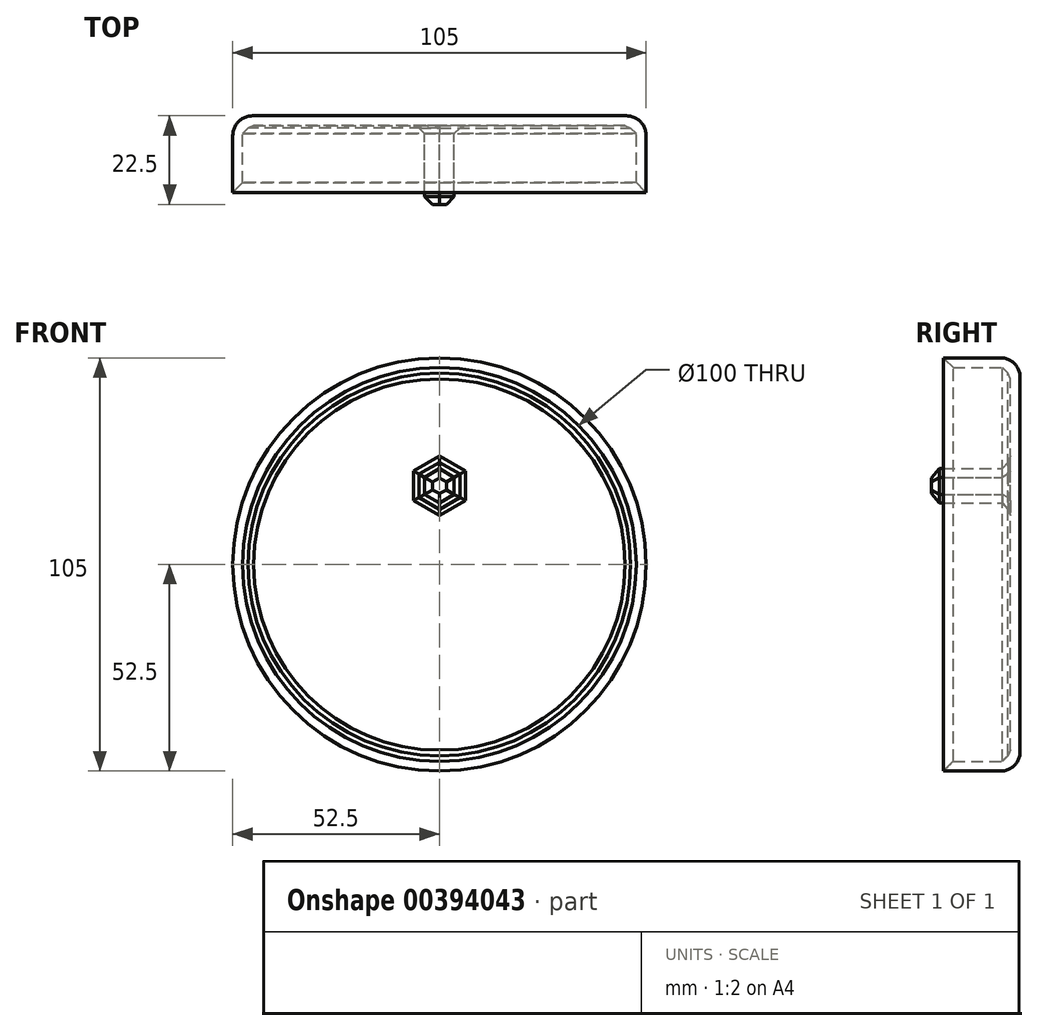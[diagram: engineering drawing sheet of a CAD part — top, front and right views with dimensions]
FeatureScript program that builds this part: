
annotation { "Feature Type Name" : "Feature", "Feature Type Description" : "" }
export const myFeature = defineFeature(function(context is Context, id is Id, definition is map)
    precondition{}
    {
        {
            var Q0;
            Q0=qCreatedBy(makeId("Front.planeOp"),FACE);
            var sketch = newSketch(context, id + "F0", { "sketchPlane" : qUnion([Q0])});
            skCircle(sketch, "E0", {"center": v(0, 0) * mm, "radius": 52.5 * mm});
            skSolve(sketch);
        }
        {
            var Q0;
            Q0 = qSketchRegion(id + "F0", true);
            extrude(context, id + "F1", {"entities" : qUnion([Q0]), "depth" : 20 * mm});
        }
        {
            var Q0;
            Q0=makeQuery(id+"F1.opExtrude","CAP_FACE",FACE,{"disambiguationData":[OSD([sQuery(id+"F0.wireOp",EDGE,"E0")])],"isStart":false});
            shell(context, id + "F2", {"entities" : qUnion([Q0]), "thickness" : 2.5 * mm});
        }
        {
            var Q0;
            Q0=qCreatedBy(makeId("Right.planeOp"),FACE);
            var sketch = newSketch(context, id + "F3", { "sketchPlane" : qUnion([Q0])});
            skLineSegment(sketch, "E1", {"start": v(0, 0) * mm, "end": v(-90.9, 0) * mm});
            skSolve(sketch);
        }
        {
            var Q0;
            {var subQ0=sQuery(id+"F0.wireOp",EDGE,"E0");Q0=makeQuery(id+"F2.opShell","OFFSET_FACE",FACE,{"disambiguationData":[OSD([subQ0]),TDD([makeQuery(id+"F1.opExtrude","CAP_FACE",FACE,{"disambiguationData":[OSD([subQ0])],"isStart":true})])]});}
            var sketch = newSketch(context, id + "F4", { "sketchPlane" : qUnion([Q0])});
            skCircle(sketch, "E2.cCircle", {"center": v(0, 20) * mm, "radius": 3.75 * mm, "construction": true});
            skLineSegment(sketch, "E2.0", {"start": v(3.75, 22.17) * mm, "end": v(3.75, 17.83) * mm});
            skLineSegment(sketch, "E2.1", {"start": v(3.75, 17.83) * mm, "end": v(0, 15.67) * mm});
            skLineSegment(sketch, "E2.2", {"start": v(0, 15.67) * mm, "end": v(-3.75, 17.83) * mm});
            skLineSegment(sketch, "E2.3", {"start": v(-3.75, 17.83) * mm, "end": v(-3.75, 22.17) * mm});
            skLineSegment(sketch, "E2.4", {"start": v(-3.75, 22.17) * mm, "end": v(0, 24.33) * mm});
            skLineSegment(sketch, "E2.5", {"start": v(0, 24.33) * mm, "end": v(3.75, 22.17) * mm});
            skPoint(sketch, "E2.0.midPoint", {"position": v(3.75, 20) * mm});
            skSolve(sketch);
        }
        {
            var Q0;
            Q0 = qSketchRegion(id + "F4", true);
            extrude(context, id + "F5", {"entities" : qUnion([Q0]), "operationType" : NewBodyOperationType.ADD, "depth" : 20 * mm});
        }
        {
            var Q0;
            Q0=makeQuery(id+"F5.opExtrude","CAP_EDGE",EDGE,{"disambiguationData":[OSD([sQuery(id+"F4.wireOp",EDGE,"E2.1")])],"isStart":true});
            var Q1;
            {var subQ0=sQuery(id+"F0.wireOp",EDGE,"E0");Q1=makeQuery(id+"F2.opShell","OFFSET_FACE",FACE,{"disambiguationData":[OSD([subQ0]),TDD([makeQuery(id+"F1.opExtrude","CAP_FACE",FACE,{"disambiguationData":[OSD([subQ0])],"isStart":true})])]});}
            var Q2;
            Q2=makeQuery(id+"F5.opExtrude","CAP_FACE",FACE,{"disambiguationData":[OSD([sQuery(id+"F4.wireOp",EDGE,"E2.0"),sQuery(id+"F4.wireOp",EDGE,"E2.1"),sQuery(id+"F4.wireOp",EDGE,"E2.2"),sQuery(id+"F4.wireOp",EDGE,"E2.3"),sQuery(id+"F4.wireOp",EDGE,"E2.4"),sQuery(id+"F4.wireOp",EDGE,"E2.5")])],"isStart":false});
            chamfer(context, id + "F6", {"entities" : qUnion([Q0, Q1, Q2]), "width" : 2 * mm, "tangentPropagation" : true});
        }
        {
            var Q0;
            Q0=makeQuery(id+"FJLK97BWJ1nyciQ_1.3.F5.opExtrude","CAP_FACE",FACE,{"disambiguationData":[OSD([sQuery(id+"F4.wireOp",EDGE,"E2.0"),sQuery(id+"F4.wireOp",EDGE,"E2.1"),sQuery(id+"F4.wireOp",EDGE,"E2.2"),sQuery(id+"F4.wireOp",EDGE,"E2.3"),sQuery(id+"F4.wireOp",EDGE,"E2.4"),sQuery(id+"F4.wireOp",EDGE,"E2.5")])],"isStart":false});
            var Q1;
            Q1=makeQuery(id+"FJLK97BWJ1nyciQ_1.1.F5.opExtrude","CAP_FACE",FACE,{"disambiguationData":[OSD([sQuery(id+"F4.wireOp",EDGE,"E2.0"),sQuery(id+"F4.wireOp",EDGE,"E2.1"),sQuery(id+"F4.wireOp",EDGE,"E2.2"),sQuery(id+"F4.wireOp",EDGE,"E2.3"),sQuery(id+"F4.wireOp",EDGE,"E2.4"),sQuery(id+"F4.wireOp",EDGE,"E2.5")])],"isStart":false});
            var Q2;
            Q2=makeQuery(id+"FJLK97BWJ1nyciQ_1.2.F5.opExtrude","CAP_FACE",FACE,{"disambiguationData":[OSD([sQuery(id+"F4.wireOp",EDGE,"E2.0"),sQuery(id+"F4.wireOp",EDGE,"E2.1"),sQuery(id+"F4.wireOp",EDGE,"E2.2"),sQuery(id+"F4.wireOp",EDGE,"E2.3"),sQuery(id+"F4.wireOp",EDGE,"E2.4"),sQuery(id+"F4.wireOp",EDGE,"E2.5")])],"isStart":false});
            var Q3;
            {var subQ0=sQuery(id+"F0.wireOp",EDGE,"E0");Q3=makeQuery(id+"F2.opShell","OFFSET_FACE",FACE,{"disambiguationData":[OSD([subQ0]),TDD([makeQuery(id+"F1.opExtrude","CAP_FACE",FACE,{"disambiguationData":[OSD([subQ0])],"isStart":true})])]});}
            chamfer(context, id + "F7", {"entities" : qUnion([Q0, Q1, Q2, Q3]), "width" : 2 * mm, "tangentPropagation" : true});
        }
        {
            var Q0;
            Q0=makeQuery(id+"F1.opExtrude","CAP_EDGE",EDGE,{"disambiguationData":[OSD([sQuery(id+"F0.wireOp",EDGE,"E0")])],"isStart":true});
            fillet(context, id + "F8", {"entities" : qUnion([Q0]), "radius" : 5 * mm, "tangentPropagation" : true, "allowEdgeOverflow" : false});
        }
        {
            var Q0;
            {var subQ0=sQuery(id+"F0.wireOp",EDGE,"E0");Q0=makeQuery(id+"F2.opShell","OFFSET_EDGE",EDGE,{"disambiguationData":[OSD([subQ0]),TDD([makeQuery(id+"F1.opExtrude","CAP_EDGE",EDGE,{"disambiguationData":[OSD([subQ0])],"isStart":false})])]});}
            chamfer(context, id + "F9", {"entities" : qUnion([Q0]), "width" : 3 * mm, "tangentPropagation" : true});
        }
    });
